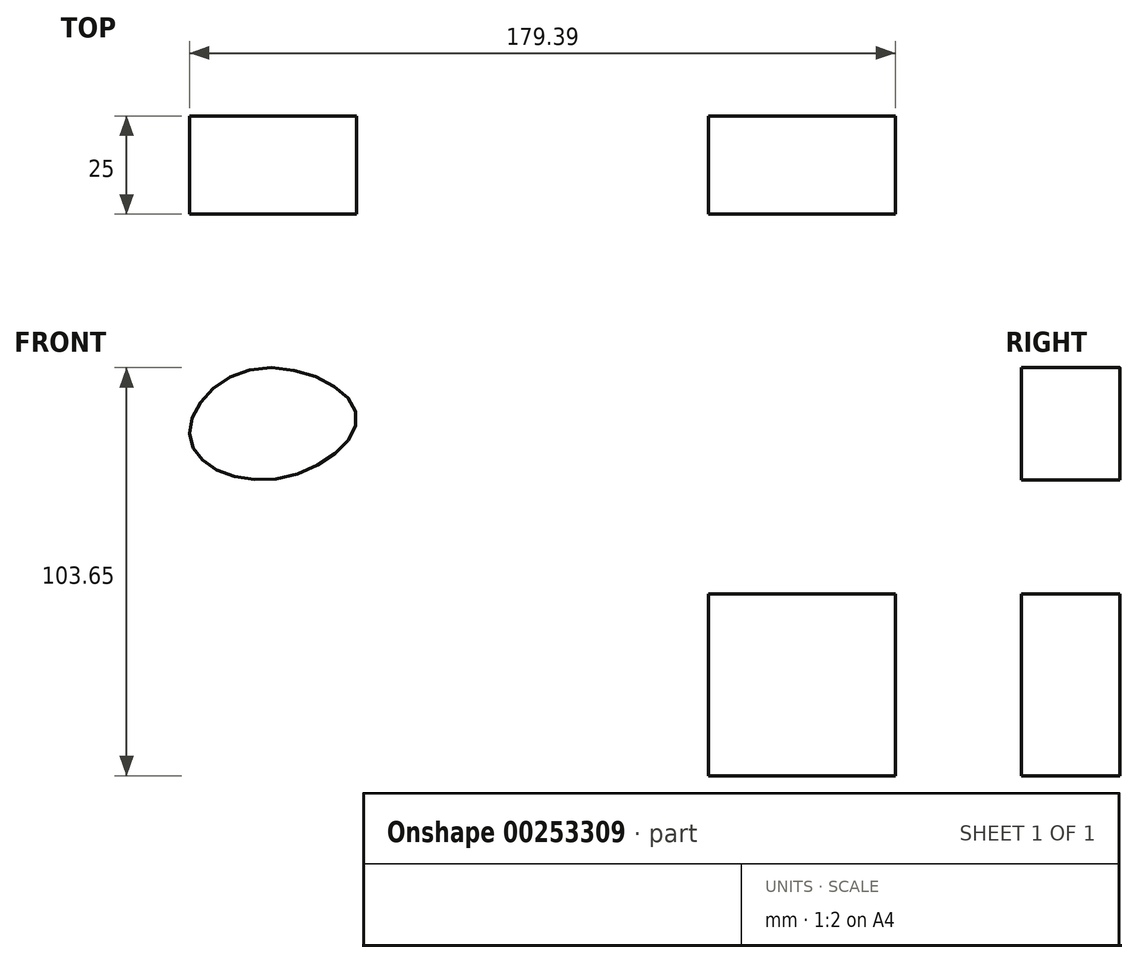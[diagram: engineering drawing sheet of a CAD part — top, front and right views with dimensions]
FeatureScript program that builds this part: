
annotation { "Feature Type Name" : "Feature", "Feature Type Description" : "" }
export const myFeature = defineFeature(function(context is Context, id is Id, definition is map)
    precondition{}
    {
        {
            var Q0;
            Q0=qCreatedBy(makeId("Front.planeOp"),FACE);
            var sketch = newSketch(context, id + "F0", { "sketchPlane" : qUnion([Q0])});
            skLineSegment(sketch, "E0.bottom", {"start": v(-206.05, -38.84) * mm, "end": v(-158.55, -38.84) * mm});
            skLineSegment(sketch, "E0.top", {"start": v(-206.05, -85.08) * mm, "end": v(-158.55, -85.08) * mm});
            skLineSegment(sketch, "E0.left", {"start": v(-206.05, -38.84) * mm, "end": v(-206.05, -85.08) * mm});
            skLineSegment(sketch, "E0.right", {"start": v(-158.55, -38.84) * mm, "end": v(-158.55, -85.08) * mm});
            skSolve(sketch);
        }
        {
            var Q0;
            Q0 = qSketchRegion(id + "F0", true);
            extrude(context, id + "F1", {"entities" : qUnion([Q0]), "depth" : 25 * mm});
        }
        {
            var Q0;
            Q0=qCreatedBy(makeId("Front.planeOp"),FACE);
            var sketch = newSketch(context, id + "F2", { "sketchPlane" : qUnion([Q0])});
            skFitSpline(sketch, "E1", {"points": [v(-322.65, 18.03) * mm, v(-337.7, 0) * mm, v(-315.3, -9.58) * mm, v(-295.62, 6.9) * mm, v(-322.65, 18.03) * mm]});
            skSolve(sketch);
        }
        {
            var Q0;
            Q0 = qSketchRegion(id + "F2", true);
            extrude(context, id + "F3", {"entities" : qUnion([Q0]), "depth" : 25 * mm});
        }
    });
